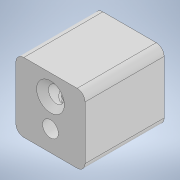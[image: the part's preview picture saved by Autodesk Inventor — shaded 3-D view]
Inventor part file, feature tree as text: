
AUTODESK INVENTOR PART (.ipt)
format: ipt  version: 2022 (Build 260153000, 153)  size: 11,771,904 bytes
history: native  units: mm
features: sketch x6, extrude x4, other x3, projected_geometry x2, direct_edit x1, revolve x1, sweep x1, chamfer x1, plane x1, mirror x1, fillet x1, boolean_combine x1, draft x1, hole x1
ambient origin geometry x8: Origin, YZ Plane, XZ Plane, XY Plane, X Axis, Y Axis, Z Axis, Center Point
bodies: Solid1 (feature_tree), Solid2 (feature_tree), Solid3 (feature_tree)
feature tree (25):
  other  "chess_pawn"
  other  "MeshFeature1"
  direct_edit  "Direct Edit1"
  sketch  "Sketch1"  dims[d0=7.8mm d1=10.0mm d2=10.0mm d3=35.0mm]
  extrude  "Extrusion1"  Depth=35.0mm
  revolve  "Revolution1"  [1 undecoded]
  sweep  "Sweep1"
  chamfer  "Chamfer1"  Distance=35.0mm
  plane  "Work Plane1"
  mirror  "Mirror1"
  extrude  "Extrusion2"  TaperAngle=90.0deg  [1 undecoded]
  extrude  "Extrusion3"  Depth=8.0mm
  fillet  "Fillet1"  [1 undecoded]
  extrude  "Extrusion4"  Depth=2.0mm TaperAngle=45.0deg
  boolean_combine  "Combine1"
  draft  "FaceDraft1"
  hole  "Hole1"  [1 undecoded]
  sketch  "Sketch2"  dims[d5=40.0mm d6=9.5mm]
  sketch  "Sketch3"  dims[d7=3.5mm d8=15.0mm]
  sketch  "Sketch4"  dims[d9=3.0mm]
  sketch  "Sketch5"  dims[d10=13.5mm]
  projected_geometry  "Projected Loop1"
  sketch  "Sketch6"  dims[d11=31.0mm d12=35.0mm d13=0.0mm d14=90.0deg d15=8.0mm d16=0.0mm d17=0.0mm d18=3.0mm d19=2.0mm d20=45.0deg d23=3.25mm d24=0.0mm d25=3.25mm d26=0.0mm d27=4.0mm d28=0.0mm d29=4.0mm d30=-0.872665mm d31=4.0mm d32=6.0mm d33=6.5mm d34=10.0mm d35=90.0deg d36=24.0mm d37=0.0mm]
  projected_geometry  "Projected Loop2"
  other  "Scale1"
note: 4 required parameter values undecoded (feature->parameter linkage not recoverable at this tier; creation-order binding heuristic only, values carry confidence <= 0.55)